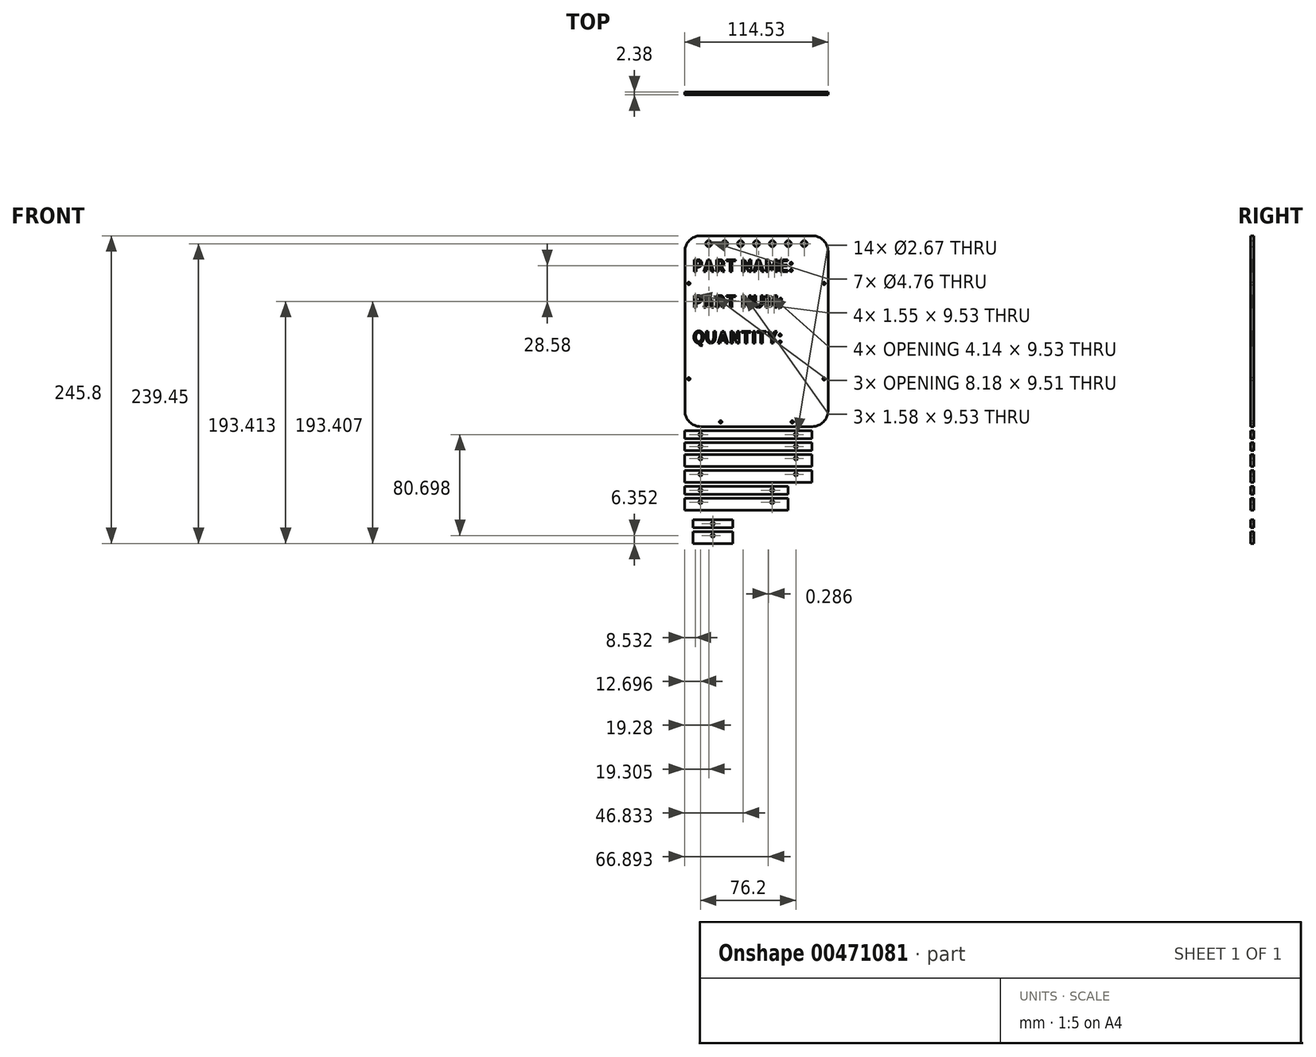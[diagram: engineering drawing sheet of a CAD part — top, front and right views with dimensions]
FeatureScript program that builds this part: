
annotation { "Feature Type Name" : "Feature", "Feature Type Description" : "" }
export const myFeature = defineFeature(function(context is Context, id is Id, definition is map)
    precondition{}
    {
        {
            var Q0;
            Q0=qCreatedBy(makeId("Front.planeOp"),FACE);
            var sketch = newSketch(context, id + "F0", { "sketchPlane" : qUnion([Q0])});
            skLineSegment(sketch, "E0.bottom", {"start": v(-44.45, 76.2) * mm, "end": v(44.45, 76.2) * mm});
            skLineSegment(sketch, "E0.top", {"start": v(-44.45, -76.2) * mm, "end": v(44.45, -76.2) * mm});
            skLineSegment(sketch, "E0.left", {"start": v(-57.15, 63.5) * mm, "end": v(-57.15, -63.5) * mm});
            skLineSegment(sketch, "E0.right", {"start": v(57.15, 63.5) * mm, "end": v(57.15, -63.5) * mm});
            skPoint(sketch, "E1.visualSharp", {"position": v(-57.15, 76.2) * mm});
            skArc(sketch, "E1.filletArc", {"start": v(-44.45, 76.2) * mm, "mid": v(-53.43, 72.48) * mm, "end": v(-57.15, 63.5) * mm});
            skPoint(sketch, "E2.visualSharp", {"position": v(57.15, 76.2) * mm});
            skArc(sketch, "E2.filletArc", {"start": v(57.15, 63.5) * mm, "mid": v(53.43, 72.48) * mm, "end": v(44.45, 76.2) * mm});
            skPoint(sketch, "E3.visualSharp", {"position": v(57.15, -76.2) * mm});
            skArc(sketch, "E3.filletArc", {"start": v(44.45, -76.2) * mm, "mid": v(53.43, -72.48) * mm, "end": v(57.15, -63.5) * mm});
            skPoint(sketch, "E4.visualSharp", {"position": v(-57.15, -76.2) * mm});
            skArc(sketch, "E4.filletArc", {"start": v(-57.15, -63.5) * mm, "mid": v(-53.43, -72.48) * mm, "end": v(-44.45, -76.2) * mm});
            skText(sketch, "E5", { "text": "PART NAME:", "fontName": "AllertaStencil-Regular.ttf"});
            skText(sketch, "E6", { "text": "PART NUM:", "fontName": "AllertaStencil-Regular.ttf"});
            skText(sketch, "E7", { "text": "QUANTITY:", "fontName": "AllertaStencil-Regular.ttf"});
            skPoint(sketch, "E8", {"position": v(0, 69.85) * mm});
            skPoint(sketch, "E9", {"position": v(-12.7, 69.85) * mm});
            skPoint(sketch, "E10", {"position": v(-25.4, 69.85) * mm});
            skPoint(sketch, "E11", {"position": v(-38.1, 69.85) * mm});
            skPoint(sketch, "E12", {"position": v(12.7, 69.85) * mm});
            skPoint(sketch, "E13", {"position": v(25.4, 69.85) * mm});
            skPoint(sketch, "E14", {"position": v(38.1, 69.85) * mm});
            skPoint(sketch, "E15", {"position": v(0, -76.2) * mm});
            skPoint(sketch, "E16", {"position": v(57.15, 0) * mm});
            skCircle(sketch, "E17", {"center": v(-38.1, 69.85) * mm, "radius": 2.38 * mm});
            skCircle(sketch, "E18", {"center": v(-25.4, 69.85) * mm, "radius": 2.38 * mm});
            skCircle(sketch, "E19", {"center": v(-12.7, 69.85) * mm, "radius": 2.38 * mm});
            skCircle(sketch, "E20", {"center": v(0, 69.85) * mm, "radius": 2.38 * mm});
            skCircle(sketch, "E21", {"center": v(12.7, 69.85) * mm, "radius": 2.38 * mm});
            skCircle(sketch, "E22", {"center": v(25.4, 69.85) * mm, "radius": 2.38 * mm});
            skCircle(sketch, "E23", {"center": v(38.1, 69.85) * mm, "radius": 2.38 * mm});
            skPoint(sketch, "E24", {"position": v(-53.97, 38.1) * mm});
            skPoint(sketch, "E25", {"position": v(-53.97, -38.1) * mm});
            skPoint(sketch, "E26", {"position": v(53.98, 38.1) * mm});
            skPoint(sketch, "E27", {"position": v(53.98, -38.1) * mm});
            skCircle(sketch, "E28", {"center": v(-53.97, 38.1) * mm, "radius": 1 * mm});
            skCircle(sketch, "E29", {"center": v(53.98, 38.1) * mm, "radius": 1 * mm});
            skCircle(sketch, "E30", {"center": v(53.98, -38.1) * mm, "radius": 1 * mm});
            skCircle(sketch, "E31", {"center": v(-53.97, -38.1) * mm, "radius": 1 * mm});
            skPoint(sketch, "E32", {"position": v(-28.58, -72.49) * mm});
            skPoint(sketch, "E33", {"position": v(28.58, -72.49) * mm});
            skCircle(sketch, "E34", {"center": v(-28.58, -72.49) * mm, "radius": 1 * mm});
            skCircle(sketch, "E35", {"center": v(28.58, -72.49) * mm, "radius": 1 * mm});
            skLineSegment(sketch, "E36.bottom", {"start": v(-57.38, -79.38) * mm, "end": v(44.22, -79.38) * mm});
            skLineSegment(sketch, "E36.top", {"start": v(-57.38, -85.72) * mm, "end": v(44.22, -85.72) * mm});
            skLineSegment(sketch, "E36.left", {"start": v(-57.38, -79.38) * mm, "end": v(-57.38, -85.72) * mm});
            skLineSegment(sketch, "E36.right", {"start": v(44.22, -79.38) * mm, "end": v(44.22, -85.72) * mm});
            skLineSegment(sketch, "E37.bottom", {"start": v(-57.38, -88.9) * mm, "end": v(44.22, -88.9) * mm});
            skLineSegment(sketch, "E37.top", {"start": v(-57.38, -95.25) * mm, "end": v(44.22, -95.25) * mm});
            skLineSegment(sketch, "E37.left", {"start": v(-57.38, -88.9) * mm, "end": v(-57.38, -95.25) * mm});
            skLineSegment(sketch, "E37.right", {"start": v(44.22, -88.9) * mm, "end": v(44.22, -95.25) * mm});
            skCircle(sketch, "E38", {"center": v(-44.68, -82.55) * mm, "radius": 1.33 * mm});
            skCircle(sketch, "E39", {"center": v(31.52, -82.55) * mm, "radius": 1.33 * mm});
            skCircle(sketch, "E40", {"center": v(-44.68, -92.07) * mm, "radius": 1.33 * mm});
            skPoint(sketch, "E40.centerSnap0", {"position": v(-57.38, -92.07) * mm});
            skCircle(sketch, "E41", {"center": v(31.52, -92.07) * mm, "radius": 1.33 * mm});
            skLineSegment(sketch, "E42.bottom", {"start": v(-57.38, -98.42) * mm, "end": v(44.22, -98.42) * mm});
            skLineSegment(sketch, "E42.top", {"start": v(-57.38, -107.95) * mm, "end": v(44.22, -107.95) * mm});
            skLineSegment(sketch, "E42.left", {"start": v(-57.38, -98.42) * mm, "end": v(-57.38, -107.95) * mm});
            skLineSegment(sketch, "E42.right", {"start": v(44.22, -98.42) * mm, "end": v(44.22, -107.95) * mm});
            skLineSegment(sketch, "E43.bottom", {"start": v(-57.38, -111.12) * mm, "end": v(44.22, -111.12) * mm});
            skLineSegment(sketch, "E43.top", {"start": v(-57.38, -120.65) * mm, "end": v(44.22, -120.65) * mm});
            skLineSegment(sketch, "E43.left", {"start": v(-57.38, -111.12) * mm, "end": v(-57.38, -120.65) * mm});
            skLineSegment(sketch, "E43.right", {"start": v(44.22, -111.12) * mm, "end": v(44.22, -120.65) * mm});
            skPoint(sketch, "E44", {"position": v(-57.38, -81.98) * mm});
            skPoint(sketch, "E45", {"position": v(-57.38, -101.6) * mm});
            skPoint(sketch, "E46", {"position": v(-57.38, -114.3) * mm});
            skCircle(sketch, "E47", {"center": v(-44.68, -101.6) * mm, "radius": 1.33 * mm});
            skCircle(sketch, "E48", {"center": v(31.52, -101.6) * mm, "radius": 1.33 * mm});
            skCircle(sketch, "E49", {"center": v(-44.68, -114.3) * mm, "radius": 1.33 * mm});
            skCircle(sketch, "E50", {"center": v(31.52, -114.3) * mm, "radius": 1.33 * mm});
            skLineSegment(sketch, "E51.bottom", {"start": v(-57.38, -123.82) * mm, "end": v(25.17, -123.82) * mm});
            skLineSegment(sketch, "E51.top", {"start": v(-57.38, -130.17) * mm, "end": v(25.17, -130.17) * mm});
            skLineSegment(sketch, "E51.left", {"start": v(-57.38, -123.82) * mm, "end": v(-57.38, -130.17) * mm});
            skLineSegment(sketch, "E51.right", {"start": v(25.17, -123.82) * mm, "end": v(25.17, -130.17) * mm});
            skLineSegment(sketch, "E52.bottom", {"start": v(-57.38, -133.35) * mm, "end": v(25.17, -133.35) * mm});
            skLineSegment(sketch, "E52.top", {"start": v(-57.38, -142.88) * mm, "end": v(25.17, -142.88) * mm});
            skLineSegment(sketch, "E52.left", {"start": v(-57.38, -133.35) * mm, "end": v(-57.38, -142.88) * mm});
            skLineSegment(sketch, "E52.right", {"start": v(25.17, -133.35) * mm, "end": v(25.17, -142.88) * mm});
            skCircle(sketch, "E53", {"center": v(-44.68, -127) * mm, "radius": 1.33 * mm});
            skPoint(sketch, "E53.centerSnap0", {"position": v(-57.38, -127) * mm});
            skPoint(sketch, "E54", {"position": v(-57.38, -136.53) * mm});
            skCircle(sketch, "E55", {"center": v(-44.68, -136.53) * mm, "radius": 1.33 * mm});
            skCircle(sketch, "E56", {"center": v(12.58, -127) * mm, "radius": 1.33 * mm});
            skCircle(sketch, "E57", {"center": v(12.58, -136.53) * mm, "radius": 1.33 * mm});
            skLineSegment(sketch, "E58.bottom", {"start": v(-50.74, -150.55) * mm, "end": v(-18.99, -150.55) * mm});
            skLineSegment(sketch, "E58.top", {"start": v(-50.74, -156.9) * mm, "end": v(-18.99, -156.9) * mm});
            skLineSegment(sketch, "E58.left", {"start": v(-50.74, -150.55) * mm, "end": v(-50.74, -156.9) * mm});
            skLineSegment(sketch, "E58.right", {"start": v(-18.99, -150.55) * mm, "end": v(-18.99, -156.9) * mm});
            skLineSegment(sketch, "E59.bottom", {"start": v(-50.74, -160.07) * mm, "end": v(-18.99, -160.07) * mm});
            skLineSegment(sketch, "E59.top", {"start": v(-50.74, -169.6) * mm, "end": v(-18.99, -169.6) * mm});
            skLineSegment(sketch, "E59.left", {"start": v(-50.74, -160.07) * mm, "end": v(-50.74, -169.6) * mm});
            skLineSegment(sketch, "E59.right", {"start": v(-18.99, -160.07) * mm, "end": v(-18.99, -169.6) * mm});
            skPoint(sketch, "E60.centerSnap0", {"position": v(-50.74, -153.72) * mm});
            skPoint(sketch, "E61", {"position": v(-50.74, -163.25) * mm});
            skPoint(sketch, "E62", {"position": v(-34.86, -150.55) * mm});
            skCircle(sketch, "E63", {"center": v(-34.86, -153.72) * mm, "radius": 1.33 * mm});
            skCircle(sketch, "E64", {"center": v(-34.86, -163.25) * mm, "radius": 1.33 * mm});
            const initialGuessF0  = {"E5": [-0.0508, 0.04763, 1, 0, 0.00953], "E6": [-0.0508, 0.01905, 1, 0, 0.00953], "E7": [-0.0508, -0.00952, 1, 0, 0.00952]};
            skSetInitialGuess(sketch, initialGuessF0);
            skSolve(sketch);
        }
        {
            var Q0;
            Q0 = qSketchRegion(id + "F0", true);
            extrude(context, id + "F1", {"entities" : qUnion([Q0]), "depth" : 2.38 * mm});
        }
    });
